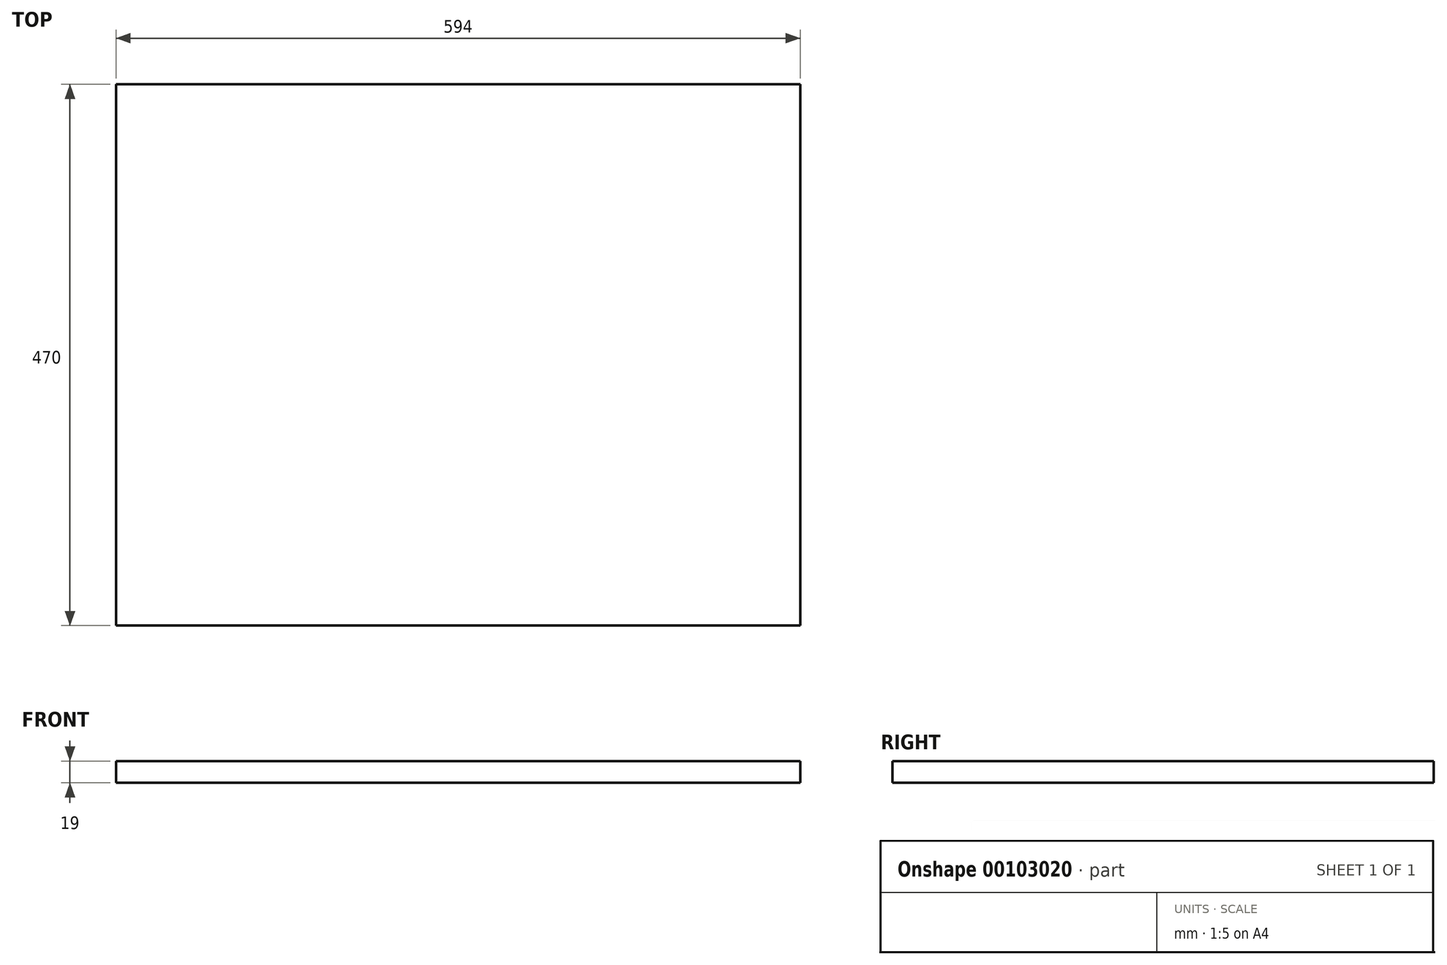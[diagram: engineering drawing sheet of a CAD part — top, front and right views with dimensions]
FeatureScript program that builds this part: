
annotation { "Feature Type Name" : "Feature", "Feature Type Description" : "" }
export const myFeature = defineFeature(function(context is Context, id is Id, definition is map)
    precondition{}
    {
        {
            var Q0;
            Q0=qCreatedBy(makeId("Top.planeOp"),FACE);
            var sketch = newSketch(context, id + "F0", { "sketchPlane" : qUnion([Q0])});
            skLineSegment(sketch, "E0.bottom", {"start": v(-70.96, 65.05) * mm, "end": v(523.04, 65.05) * mm});
            skLineSegment(sketch, "E0.top", {"start": v(-70.96, -404.95) * mm, "end": v(523.04, -404.95) * mm});
            skLineSegment(sketch, "E0.left", {"start": v(-70.96, 65.05) * mm, "end": v(-70.96, -404.95) * mm});
            skLineSegment(sketch, "E0.right", {"start": v(523.04, 65.05) * mm, "end": v(523.04, -404.95) * mm});
            skSolve(sketch);
        }
        {
            var Q0;
            Q0=qSketchRegion(id+"F0",true);
            extrude(context, id + "F1", {"entities" : qUnion([Q0]), "depth" : 19 * mm});
        }
    });
